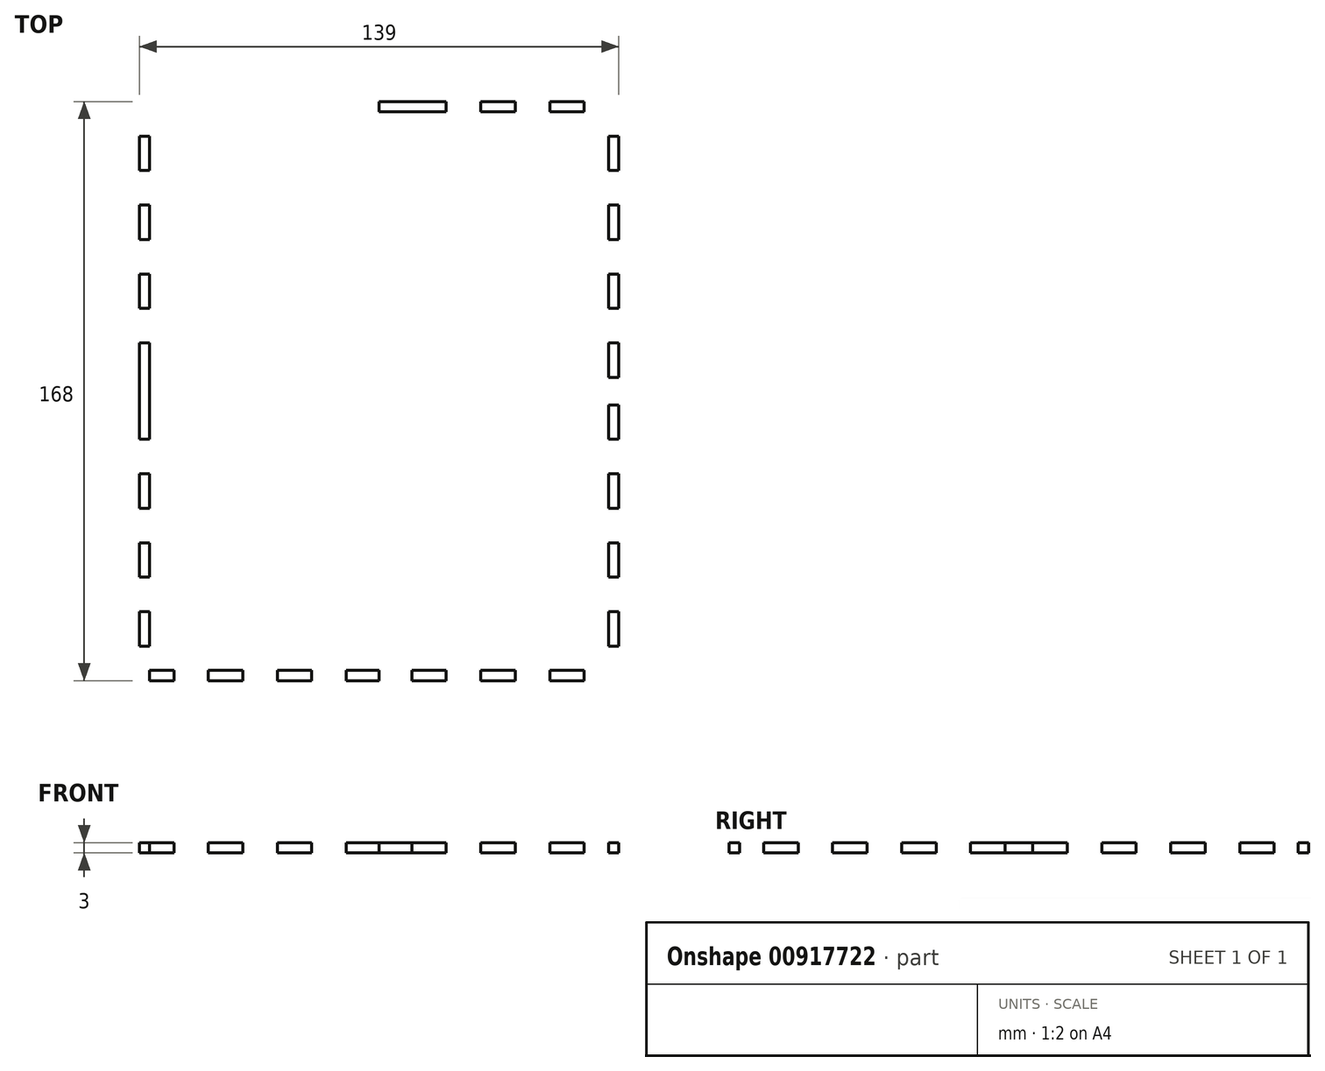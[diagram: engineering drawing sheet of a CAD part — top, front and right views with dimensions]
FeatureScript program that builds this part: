
annotation { "Feature Type Name" : "Feature", "Feature Type Description" : "" }
export const myFeature = defineFeature(function(context is Context, id is Id, definition is map)
    precondition{}
    {
        {
            var Q0;
            Q0=qCreatedBy(makeId("Top.planeOp"),FACE);
            var sketch = newSketch(context, id + "F0", { "sketchPlane" : qUnion([Q0])});
            skLineSegment(sketch, "E0.bottom", {"start": v(-69.5, 84) * mm, "end": v(0, 84) * mm});
            skLineSegment(sketch, "E0.top", {"start": v(-69.5, 0) * mm, "end": v(0, 0) * mm});
            skLineSegment(sketch, "E0.left", {"start": v(-69.5, 84) * mm, "end": v(-69.5, 0) * mm});
            skLineSegment(sketch, "E0.right", {"start": v(0, 84) * mm, "end": v(0, 0) * mm});
            skLineSegment(sketch, "E1", {"start": v(-69.5, 81) * mm, "end": v(0, 81) * mm});
            skLineSegment(sketch, "E2", {"start": v(-66.5, 84) * mm, "end": v(-66.5, 0) * mm});
            skLineSegment(sketch, "E3.bottom", {"start": v(-69.5, 84) * mm, "end": v(-59.5, 84) * mm});
            skLineSegment(sketch, "E3.top", {"start": v(-69.5, 81) * mm, "end": v(-59.5, 81) * mm});
            skLineSegment(sketch, "E3.left", {"start": v(-69.5, 84) * mm, "end": v(-69.5, 81) * mm});
            skLineSegment(sketch, "E3.right", {"start": v(-59.5, 84) * mm, "end": v(-59.5, 81) * mm});
            skLineSegment(sketch, "E4.bottom", {"start": v(-49.5, 84) * mm, "end": v(-39.5, 84) * mm});
            skLineSegment(sketch, "E4.top", {"start": v(-49.5, 81) * mm, "end": v(-39.5, 81) * mm});
            skLineSegment(sketch, "E4.left", {"start": v(-49.5, 84) * mm, "end": v(-49.5, 81) * mm});
            skLineSegment(sketch, "E4.right", {"start": v(-39.5, 84) * mm, "end": v(-39.5, 81) * mm});
            skLineSegment(sketch, "E5.bottom", {"start": v(-29.5, 84) * mm, "end": v(-19.5, 84) * mm});
            skLineSegment(sketch, "E5.top", {"start": v(-29.5, 81) * mm, "end": v(-19.5, 81) * mm});
            skLineSegment(sketch, "E5.left", {"start": v(-29.5, 84) * mm, "end": v(-29.5, 81) * mm});
            skLineSegment(sketch, "E5.right", {"start": v(-19.5, 84) * mm, "end": v(-19.5, 81) * mm});
            skLineSegment(sketch, "E6.bottom", {"start": v(-69.5, 84) * mm, "end": v(-66.5, 84) * mm});
            skLineSegment(sketch, "E6.top", {"start": v(-69.5, 74) * mm, "end": v(-66.5, 74) * mm});
            skLineSegment(sketch, "E6.left", {"start": v(-69.5, 84) * mm, "end": v(-69.5, 74) * mm});
            skLineSegment(sketch, "E6.right", {"start": v(-66.5, 84) * mm, "end": v(-66.5, 74) * mm});
            skLineSegment(sketch, "E7.bottom", {"start": v(-69.5, 64) * mm, "end": v(-66.5, 64) * mm});
            skLineSegment(sketch, "E7.top", {"start": v(-69.5, 54) * mm, "end": v(-66.5, 54) * mm});
            skLineSegment(sketch, "E7.left", {"start": v(-69.5, 64) * mm, "end": v(-69.5, 54) * mm});
            skLineSegment(sketch, "E7.right", {"start": v(-66.5, 64) * mm, "end": v(-66.5, 54) * mm});
            skLineSegment(sketch, "E8.bottom", {"start": v(-69.5, 44) * mm, "end": v(-66.5, 44) * mm});
            skLineSegment(sketch, "E8.top", {"start": v(-69.5, 34) * mm, "end": v(-66.5, 34) * mm});
            skLineSegment(sketch, "E8.left", {"start": v(-69.5, 44) * mm, "end": v(-69.5, 34) * mm});
            skLineSegment(sketch, "E8.right", {"start": v(-66.5, 44) * mm, "end": v(-66.5, 34) * mm});
            skLineSegment(sketch, "E9.bottom", {"start": v(-69.5, 24) * mm, "end": v(-66.5, 24) * mm});
            skLineSegment(sketch, "E9.top", {"start": v(-69.5, 14) * mm, "end": v(-66.5, 14) * mm});
            skLineSegment(sketch, "E9.left", {"start": v(-69.5, 24) * mm, "end": v(-69.5, 14) * mm});
            skLineSegment(sketch, "E9.right", {"start": v(-66.5, 24) * mm, "end": v(-66.5, 14) * mm});
            skLineSegment(sketch, "E10.bottom", {"start": v(-9.5, 84) * mm, "end": v(0, 84) * mm});
            skLineSegment(sketch, "E10.top", {"start": v(-9.5, 81) * mm, "end": v(0, 81) * mm});
            skLineSegment(sketch, "E10.left", {"start": v(-9.5, 84) * mm, "end": v(-9.5, 81) * mm});
            skLineSegment(sketch, "E10.right", {"start": v(0, 84) * mm, "end": v(0, 81) * mm});
            skLineSegment(sketch, "E11.MirrorCS", {"start": v(69.5, 84) * mm, "end": v(66.5, 84) * mm});
            skLineSegment(sketch, "E12.MirrorCS", {"start": v(69.5, 84) * mm, "end": v(69.5, 81) * mm});
            skLineSegment(sketch, "E13.MirrorCS", {"start": v(19.5, 84) * mm, "end": v(19.5, 81) * mm});
            skLineSegment(sketch, "E14.MirrorCS", {"start": v(69.5, 74) * mm, "end": v(66.5, 74) * mm});
            skLineSegment(sketch, "E15.MirrorCS", {"start": v(49.5, 84) * mm, "end": v(49.5, 81) * mm});
            skLineSegment(sketch, "E16.MirrorCS", {"start": v(69.5, 34) * mm, "end": v(66.5, 34) * mm});
            skLineSegment(sketch, "E17.MirrorCS", {"start": v(29.5, 84) * mm, "end": v(29.5, 81) * mm});
            skLineSegment(sketch, "E18.MirrorCS", {"start": v(69.5, 24) * mm, "end": v(66.5, 24) * mm});
            skLineSegment(sketch, "E19.MirrorCS", {"start": v(59.5, 84) * mm, "end": v(59.5, 81) * mm});
            skLineSegment(sketch, "E20.MirrorCS", {"start": v(39.5, 84) * mm, "end": v(39.5, 81) * mm});
            skLineSegment(sketch, "E21.MirrorCS", {"start": v(69.5, 54) * mm, "end": v(66.5, 54) * mm});
            skLineSegment(sketch, "E22.MirrorCS", {"start": v(69.5, 64) * mm, "end": v(66.5, 64) * mm});
            skLineSegment(sketch, "E23.MirrorCS", {"start": v(69.5, 14) * mm, "end": v(66.5, 14) * mm});
            skLineSegment(sketch, "E24.MirrorCS", {"start": v(9.5, 84) * mm, "end": v(9.5, 81) * mm});
            skLineSegment(sketch, "E25.MirrorCS", {"start": v(69.5, 44) * mm, "end": v(66.5, 44) * mm});
            skLineSegment(sketch, "E26.MirrorCS", {"start": v(69.5, 64) * mm, "end": v(69.5, 54) * mm});
            skLineSegment(sketch, "E27.MirrorCS", {"start": v(66.5, 64) * mm, "end": v(66.5, 54) * mm});
            skLineSegment(sketch, "E28.MirrorCS", {"start": v(69.5, 44) * mm, "end": v(69.5, 34) * mm});
            skLineSegment(sketch, "E29.MirrorCS", {"start": v(69.5, 84) * mm, "end": v(59.5, 84) * mm});
            skLineSegment(sketch, "E30.MirrorCS", {"start": v(29.5, 84) * mm, "end": v(19.5, 84) * mm});
            skLineSegment(sketch, "E31.MirrorCS", {"start": v(69.5, 0) * mm, "end": v(0, 0) * mm});
            skLineSegment(sketch, "E32.MirrorCS", {"start": v(69.5, 81) * mm, "end": v(0, 81) * mm});
            skLineSegment(sketch, "E33.MirrorCS", {"start": v(66.5, 84) * mm, "end": v(66.5, 0) * mm});
            skLineSegment(sketch, "E34.MirrorCS", {"start": v(9.5, 84) * mm, "end": v(0, 84) * mm});
            skLineSegment(sketch, "E35.MirrorCS", {"start": v(66.5, 24) * mm, "end": v(66.5, 14) * mm});
            skLineSegment(sketch, "E36.MirrorCS", {"start": v(49.5, 81) * mm, "end": v(39.5, 81) * mm});
            skLineSegment(sketch, "E37.MirrorCS", {"start": v(69.5, 84) * mm, "end": v(0, 84) * mm});
            skLineSegment(sketch, "E38.MirrorCS", {"start": v(29.5, 81) * mm, "end": v(19.5, 81) * mm});
            skLineSegment(sketch, "E39.MirrorCS", {"start": v(9.5, 81) * mm, "end": v(0, 81) * mm});
            skLineSegment(sketch, "E40.MirrorCS", {"start": v(49.5, 84) * mm, "end": v(39.5, 84) * mm});
            skLineSegment(sketch, "E41.MirrorCS", {"start": v(69.5, 84) * mm, "end": v(69.5, 0) * mm});
            skLineSegment(sketch, "E42.MirrorCS", {"start": v(69.5, 24) * mm, "end": v(69.5, 14) * mm});
            skLineSegment(sketch, "E43.MirrorCS", {"start": v(66.5, 84) * mm, "end": v(66.5, 74) * mm});
            skLineSegment(sketch, "E44.MirrorCS", {"start": v(69.5, 84) * mm, "end": v(69.5, 74) * mm});
            skLineSegment(sketch, "E45.MirrorCS", {"start": v(66.5, 44) * mm, "end": v(66.5, 34) * mm});
            skLineSegment(sketch, "E46.MirrorCS", {"start": v(69.5, 81) * mm, "end": v(59.5, 81) * mm});
            skLineSegment(sketch, "E47.bottom", {"start": v(-69.5, 4) * mm, "end": v(-66.5, 4) * mm});
            skLineSegment(sketch, "E47.top", {"start": v(-69.5, 0) * mm, "end": v(-66.5, 0) * mm});
            skLineSegment(sketch, "E47.left", {"start": v(-69.5, 4) * mm, "end": v(-69.5, 0) * mm});
            skLineSegment(sketch, "E47.right", {"start": v(-66.5, 4) * mm, "end": v(-66.5, 0) * mm});
            skLineSegment(sketch, "E48.MirrorCS", {"start": v(69.5, 4) * mm, "end": v(69.5, 0) * mm});
            skLineSegment(sketch, "E49.MirrorCS", {"start": v(69.5, 0) * mm, "end": v(66.5, 0) * mm});
            skLineSegment(sketch, "E50.MirrorCS", {"start": v(66.5, 4) * mm, "end": v(66.5, 0) * mm});
            skLineSegment(sketch, "E51.MirrorCS", {"start": v(69.5, 4) * mm, "end": v(66.5, 4) * mm});
            skLineSegment(sketch, "E52.MirrorCS", {"start": v(0, -84) * mm, "end": v(0, -81) * mm});
            skLineSegment(sketch, "E53.MirrorCS", {"start": v(-69.5, -84) * mm, "end": v(-69.5, -81) * mm});
            skLineSegment(sketch, "E54.MirrorCS", {"start": v(-69.5, -84) * mm, "end": v(-66.5, -84) * mm});
            skLineSegment(sketch, "E55.MirrorCS", {"start": v(69.5, -84) * mm, "end": v(69.5, -81) * mm});
            skLineSegment(sketch, "E56.MirrorCS", {"start": v(69.5, -84) * mm, "end": v(66.5, -84) * mm});
            skLineSegment(sketch, "E57.MirrorCS", {"start": v(-39.5, -84) * mm, "end": v(-39.5, -81) * mm});
            skLineSegment(sketch, "E58.MirrorCS", {"start": v(69.5, -34) * mm, "end": v(66.5, -34) * mm});
            skLineSegment(sketch, "E59.MirrorCS", {"start": v(69.5, -54) * mm, "end": v(66.5, -54) * mm});
            skLineSegment(sketch, "E60.MirrorCS", {"start": v(66.5, -4) * mm, "end": v(66.5, 0) * mm});
            skLineSegment(sketch, "E61.MirrorCS", {"start": v(39.5, -84) * mm, "end": v(39.5, -81) * mm});
            skLineSegment(sketch, "E62.MirrorCS", {"start": v(69.5, -64) * mm, "end": v(66.5, -64) * mm});
            skLineSegment(sketch, "E63.MirrorCS", {"start": v(59.5, -84) * mm, "end": v(59.5, -81) * mm});
            skLineSegment(sketch, "E64.MirrorCS", {"start": v(19.5, -84) * mm, "end": v(19.5, -81) * mm});
            skLineSegment(sketch, "E65.MirrorCS", {"start": v(-66.5, -4) * mm, "end": v(-66.5, 0) * mm});
            skLineSegment(sketch, "E66.MirrorCS", {"start": v(-69.5, -44) * mm, "end": v(-66.5, -44) * mm});
            skLineSegment(sketch, "E67.MirrorCS", {"start": v(69.5, -4) * mm, "end": v(66.5, -4) * mm});
            skLineSegment(sketch, "E68.MirrorCS", {"start": v(-69.5, -74) * mm, "end": v(-66.5, -74) * mm});
            skLineSegment(sketch, "E69.MirrorCS", {"start": v(9.5, -84) * mm, "end": v(9.5, -81) * mm});
            skLineSegment(sketch, "E70.MirrorCS", {"start": v(29.5, -84) * mm, "end": v(29.5, -81) * mm});
            skLineSegment(sketch, "E71.MirrorCS", {"start": v(-29.5, -84) * mm, "end": v(-29.5, -81) * mm});
            skLineSegment(sketch, "E72.MirrorCS", {"start": v(-69.5, -64) * mm, "end": v(-66.5, -64) * mm});
            skLineSegment(sketch, "E73.MirrorCS", {"start": v(-59.5, -84) * mm, "end": v(-59.5, -81) * mm});
            skLineSegment(sketch, "E74.MirrorCS", {"start": v(69.5, -44) * mm, "end": v(66.5, -44) * mm});
            skLineSegment(sketch, "E75.MirrorCS", {"start": v(69.5, -4) * mm, "end": v(69.5, 0) * mm});
            skLineSegment(sketch, "E76.MirrorCS", {"start": v(-69.5, -4) * mm, "end": v(-69.5, 0) * mm});
            skLineSegment(sketch, "E77.MirrorCS", {"start": v(-69.5, -4) * mm, "end": v(-66.5, -4) * mm});
            skLineSegment(sketch, "E78.MirrorCS", {"start": v(-19.5, -84) * mm, "end": v(-19.5, -81) * mm});
            skLineSegment(sketch, "E79.MirrorCS", {"start": v(69.5, -14) * mm, "end": v(66.5, -14) * mm});
            skLineSegment(sketch, "E80.MirrorCS", {"start": v(-69.5, -54) * mm, "end": v(-66.5, -54) * mm});
            skLineSegment(sketch, "E81.MirrorCS", {"start": v(-9.5, -84) * mm, "end": v(-9.5, -81) * mm});
            skLineSegment(sketch, "E82.MirrorCS", {"start": v(69.5, -24) * mm, "end": v(66.5, -24) * mm});
            skLineSegment(sketch, "E83.MirrorCS", {"start": v(69.5, -74) * mm, "end": v(66.5, -74) * mm});
            skLineSegment(sketch, "E84.MirrorCS", {"start": v(-69.5, -24) * mm, "end": v(-66.5, -24) * mm});
            skLineSegment(sketch, "E85.MirrorCS", {"start": v(-49.5, -84) * mm, "end": v(-49.5, -81) * mm});
            skLineSegment(sketch, "E86.MirrorCS", {"start": v(-69.5, -14) * mm, "end": v(-66.5, -14) * mm});
            skLineSegment(sketch, "E87.MirrorCS", {"start": v(49.5, -84) * mm, "end": v(49.5, -81) * mm});
            skLineSegment(sketch, "E88.MirrorCS", {"start": v(-69.5, -34) * mm, "end": v(-66.5, -34) * mm});
            skLineSegment(sketch, "E89.MirrorCS", {"start": v(-69.5, -64) * mm, "end": v(-69.5, -54) * mm});
            skLineSegment(sketch, "E90.MirrorCS", {"start": v(69.5, -44) * mm, "end": v(69.5, -34) * mm});
            skLineSegment(sketch, "E91.MirrorCS", {"start": v(69.5, -24) * mm, "end": v(69.5, -14) * mm});
            skLineSegment(sketch, "E92.MirrorCS", {"start": v(69.5, -84) * mm, "end": v(59.5, -84) * mm});
            skLineSegment(sketch, "E93.MirrorCS", {"start": v(66.5, -64) * mm, "end": v(66.5, -54) * mm});
            skLineSegment(sketch, "E94.MirrorCS", {"start": v(66.5, -84) * mm, "end": v(66.5, -74) * mm});
            skLineSegment(sketch, "E95.MirrorCS", {"start": v(29.5, -84) * mm, "end": v(19.5, -84) * mm});
            skLineSegment(sketch, "E96.MirrorCS", {"start": v(66.5, -44) * mm, "end": v(66.5, -34) * mm});
            skLineSegment(sketch, "E97.MirrorCS", {"start": v(49.5, -84) * mm, "end": v(39.5, -84) * mm});
            skLineSegment(sketch, "E98.MirrorCS", {"start": v(69.5, -84) * mm, "end": v(69.5, -74) * mm});
            skLineSegment(sketch, "E99.MirrorCS", {"start": v(-66.5, -64) * mm, "end": v(-66.5, -54) * mm});
            skLineSegment(sketch, "E100.MirrorCS", {"start": v(69.5, -64) * mm, "end": v(69.5, -54) * mm});
            skLineSegment(sketch, "E101.MirrorCS", {"start": v(9.5, -84) * mm, "end": v(0, -84) * mm});
            skLineSegment(sketch, "E102.MirrorCS", {"start": v(-69.5, -44) * mm, "end": v(-69.5, -34) * mm});
            skLineSegment(sketch, "E103.MirrorCS", {"start": v(-29.5, -84) * mm, "end": v(-19.5, -84) * mm});
            skLineSegment(sketch, "E104.MirrorCS", {"start": v(-29.5, -81) * mm, "end": v(-19.5, -81) * mm});
            skLineSegment(sketch, "E105.MirrorCS", {"start": v(49.5, -81) * mm, "end": v(39.5, -81) * mm});
            skLineSegment(sketch, "E106.MirrorCS", {"start": v(-69.5, -84) * mm, "end": v(0, -84) * mm});
            skLineSegment(sketch, "E107.MirrorCS", {"start": v(-66.5, -44) * mm, "end": v(-66.5, -34) * mm});
            skLineSegment(sketch, "E108.MirrorCS", {"start": v(29.5, -81) * mm, "end": v(19.5, -81) * mm});
            skLineSegment(sketch, "E109.MirrorCS", {"start": v(-66.5, -84) * mm, "end": v(-66.5, -74) * mm});
            skLineSegment(sketch, "E110.MirrorCS", {"start": v(-9.5, -81) * mm, "end": v(0, -81) * mm});
            skLineSegment(sketch, "E111.MirrorCS", {"start": v(69.5, -81) * mm, "end": v(0, -81) * mm});
            skLineSegment(sketch, "E112.MirrorCS", {"start": v(-69.5, -84) * mm, "end": v(-69.5, 0) * mm});
            skLineSegment(sketch, "E113.MirrorCS", {"start": v(-49.5, -84) * mm, "end": v(-39.5, -84) * mm});
            skLineSegment(sketch, "E114.MirrorCS", {"start": v(9.5, -81) * mm, "end": v(0, -81) * mm});
            skLineSegment(sketch, "E115.MirrorCS", {"start": v(66.5, -84) * mm, "end": v(66.5, 0) * mm});
            skLineSegment(sketch, "E116.MirrorCS", {"start": v(69.5, -84) * mm, "end": v(0, -84) * mm});
            skLineSegment(sketch, "E117.MirrorCS", {"start": v(-9.5, -84) * mm, "end": v(0, -84) * mm});
            skLineSegment(sketch, "E118.MirrorCS", {"start": v(0, -84) * mm, "end": v(0, 0) * mm});
            skLineSegment(sketch, "E119.MirrorCS", {"start": v(-69.5, -81) * mm, "end": v(0, -81) * mm});
            skLineSegment(sketch, "E120.MirrorCS", {"start": v(-49.5, -81) * mm, "end": v(-39.5, -81) * mm});
            skLineSegment(sketch, "E121.MirrorCS", {"start": v(66.5, -24) * mm, "end": v(66.5, -14) * mm});
            skLineSegment(sketch, "E122.MirrorCS", {"start": v(-66.5, -24) * mm, "end": v(-66.5, -14) * mm});
            skLineSegment(sketch, "E123.MirrorCS", {"start": v(-69.5, -24) * mm, "end": v(-69.5, -14) * mm});
            skLineSegment(sketch, "E124.MirrorCS", {"start": v(-69.5, -84) * mm, "end": v(-59.5, -84) * mm});
            skLineSegment(sketch, "E125.MirrorCS", {"start": v(69.5, -81) * mm, "end": v(59.5, -81) * mm});
            skLineSegment(sketch, "E126.MirrorCS", {"start": v(-66.5, -84) * mm, "end": v(-66.5, 0) * mm});
            skLineSegment(sketch, "E127.MirrorCS", {"start": v(69.5, -84) * mm, "end": v(69.5, 0) * mm});
            skLineSegment(sketch, "E128.MirrorCS", {"start": v(-69.5, -84) * mm, "end": v(-69.5, -74) * mm});
            skLineSegment(sketch, "E129.MirrorCS", {"start": v(-69.5, -81) * mm, "end": v(-59.5, -81) * mm});
            skSolve(sketch);
        }
        {
            var Q0;
            Q0=makeQuery(id+"F0.imprint","IMPRINT",FACE,{"disambiguationData":[TD([[makeQuery(id+"F0.imprint","IMPRINT",EDGE,{"derivedFrom":sQuery(id+"F0.wireOp",EDGE,"E0.top")}),1.0]])]});
            var Q1;
            {var subQ10=sQuery(id+"F0.wireOp",EDGE,"E0.right");Q1=makeQuery(id+"F0.imprint","IMPRINT",FACE,{"disambiguationData":[TD([[makeQuery(id+"F0.imprint","IMPRINT",EDGE,{"derivedFrom":subQ10}),1.0]])]});}
            var Q2;
            {var subQ7=sQuery(id+"F0.wireOp",EDGE,"E114.MirrorCS");Q2=makeQuery(id+"F0.imprint","IMPRINT",FACE,{"disambiguationData":[TD([[makeQuery(id+"F0.imprint","IMPRINT",EDGE,{"derivedFrom":subQ7}),-1.0]])]});}
            var Q3;
            {var subQ12=sQuery(id+"F0.wireOp",EDGE,"E0.top");Q3=makeQuery(id+"F0.imprint","IMPRINT",FACE,{"disambiguationData":[TD([[makeQuery(id+"F0.imprint","IMPRINT",EDGE,{"derivedFrom":subQ12}),-1.0]])]});}
            var Q4;
            {var subQ0=sQuery(id+"F0.wireOp",EDGE,"E3.bottom");Q4=makeQuery(id+"F0.imprint","IMPRINT",FACE,{"disambiguationData":[TD([[makeQuery(id+"F0.imprint","IMPRINT",EDGE,{"derivedFrom":subQ0}),-1.0]])]});}
            var Q5;
            Q5=makeQuery(id+"F0.imprint","IMPRINT",FACE,{"disambiguationData":[TD([[makeQuery(id+"F0.imprint","IMPRINT",EDGE,{"derivedFrom":sQuery(id+"F0.wireOp",EDGE,"E4.bottom")}),-1.0]])]});
            var Q6;
            Q6=makeQuery(id+"F0.imprint","IMPRINT",FACE,{"disambiguationData":[TD([[makeQuery(id+"F0.imprint","IMPRINT",EDGE,{"derivedFrom":sQuery(id+"F0.wireOp",EDGE,"E5.bottom")}),-1.0]])]});
            var Q7;
            Q7=makeQuery(id+"F0.imprint","IMPRINT",FACE,{"disambiguationData":[TD([[makeQuery(id+"F0.imprint","IMPRINT",EDGE,{"derivedFrom":sQuery(id+"F0.wireOp",EDGE,"E10.bottom")}),-1.0]])]});
            var Q8;
            {var subQ0=sQuery(id+"F0.wireOp",EDGE,"E13.MirrorCS");Q8=makeQuery(id+"F0.imprint","IMPRINT",FACE,{"disambiguationData":[TD([[makeQuery(id+"F0.imprint","IMPRINT",EDGE,{"derivedFrom":subQ0}),-1.0]])]});}
            var Q9;
            {var subQ0=sQuery(id+"F0.wireOp",EDGE,"E17.MirrorCS");Q9=makeQuery(id+"F0.imprint","IMPRINT",FACE,{"disambiguationData":[TD([[makeQuery(id+"F0.imprint","IMPRINT",EDGE,{"derivedFrom":subQ0}),1.0]])]});}
            var Q10;
            {var subQ0=sQuery(id+"F0.wireOp",EDGE,"E15.MirrorCS");Q10=makeQuery(id+"F0.imprint","IMPRINT",FACE,{"disambiguationData":[TD([[makeQuery(id+"F0.imprint","IMPRINT",EDGE,{"derivedFrom":subQ0}),1.0]])]});}
            var Q11;
            {var subQ0=sQuery(id+"F0.wireOp",EDGE,"E14.MirrorCS");Q11=makeQuery(id+"F0.imprint","IMPRINT",FACE,{"disambiguationData":[TD([[makeQuery(id+"F0.imprint","IMPRINT",EDGE,{"derivedFrom":subQ0}),1.0]])]});}
            var Q12;
            {var subQ0=sQuery(id+"F0.wireOp",EDGE,"E6.top");Q12=makeQuery(id+"F0.imprint","IMPRINT",FACE,{"disambiguationData":[TD([[makeQuery(id+"F0.imprint","IMPRINT",EDGE,{"derivedFrom":subQ0}),-1.0]])]});}
            var Q13;
            {var subQ0=sQuery(id+"F0.wireOp",EDGE,"E7.top");Q13=makeQuery(id+"F0.imprint","IMPRINT",FACE,{"disambiguationData":[TD([[makeQuery(id+"F0.imprint","IMPRINT",EDGE,{"derivedFrom":subQ0}),-1.0]])]});}
            var Q14;
            {var subQ0=sQuery(id+"F0.wireOp",EDGE,"E8.top");Q14=makeQuery(id+"F0.imprint","IMPRINT",FACE,{"disambiguationData":[TD([[makeQuery(id+"F0.imprint","IMPRINT",EDGE,{"derivedFrom":subQ0}),-1.0]])]});}
            var Q15;
            {var subQ2=sQuery(id+"F0.wireOp",EDGE,"E9.top");Q15=makeQuery(id+"F0.imprint","IMPRINT",FACE,{"disambiguationData":[TD([[makeQuery(id+"F0.imprint","IMPRINT",EDGE,{"derivedFrom":subQ2}),-1.0]])]});}
            var Q16;
            {var subQ0=sQuery(id+"F0.wireOp",EDGE,"E77.MirrorCS");Q16=makeQuery(id+"F0.imprint","IMPRINT",FACE,{"disambiguationData":[TD([[makeQuery(id+"F0.imprint","IMPRINT",EDGE,{"derivedFrom":subQ0}),-1.0]])]});}
            var Q17;
            {var subQ0=sQuery(id+"F0.wireOp",EDGE,"E84.MirrorCS");Q17=makeQuery(id+"F0.imprint","IMPRINT",FACE,{"disambiguationData":[TD([[makeQuery(id+"F0.imprint","IMPRINT",EDGE,{"derivedFrom":subQ0}),-1.0]])]});}
            var Q18;
            {var subQ0=sQuery(id+"F0.wireOp",EDGE,"E66.MirrorCS");Q18=makeQuery(id+"F0.imprint","IMPRINT",FACE,{"disambiguationData":[TD([[makeQuery(id+"F0.imprint","IMPRINT",EDGE,{"derivedFrom":subQ0}),-1.0]])]});}
            var Q19;
            {var subQ0=sQuery(id+"F0.wireOp",EDGE,"E68.MirrorCS");Q19=makeQuery(id+"F0.imprint","IMPRINT",FACE,{"disambiguationData":[TD([[makeQuery(id+"F0.imprint","IMPRINT",EDGE,{"derivedFrom":subQ0}),1.0]])]});}
            var Q20;
            {var subQ0=sQuery(id+"F0.wireOp",EDGE,"E62.MirrorCS");Q20=makeQuery(id+"F0.imprint","IMPRINT",FACE,{"disambiguationData":[TD([[makeQuery(id+"F0.imprint","IMPRINT",EDGE,{"derivedFrom":subQ0}),1.0]])]});}
            var Q21;
            {var subQ0=sQuery(id+"F0.wireOp",EDGE,"E59.MirrorCS");Q21=makeQuery(id+"F0.imprint","IMPRINT",FACE,{"disambiguationData":[TD([[makeQuery(id+"F0.imprint","IMPRINT",EDGE,{"derivedFrom":subQ0}),-1.0]])]});}
            var Q22;
            {var subQ0=sQuery(id+"F0.wireOp",EDGE,"E58.MirrorCS");Q22=makeQuery(id+"F0.imprint","IMPRINT",FACE,{"disambiguationData":[TD([[makeQuery(id+"F0.imprint","IMPRINT",EDGE,{"derivedFrom":subQ0}),-1.0]])]});}
            var Q23;
            {var subQ0=sQuery(id+"F0.wireOp",EDGE,"E67.MirrorCS");Q23=makeQuery(id+"F0.imprint","IMPRINT",FACE,{"disambiguationData":[TD([[makeQuery(id+"F0.imprint","IMPRINT",EDGE,{"derivedFrom":subQ0}),1.0]])]});}
            var Q24;
            {var subQ0=sQuery(id+"F0.wireOp",EDGE,"E23.MirrorCS");Q24=makeQuery(id+"F0.imprint","IMPRINT",FACE,{"disambiguationData":[TD([[makeQuery(id+"F0.imprint","IMPRINT",EDGE,{"derivedFrom":subQ0}),1.0]])]});}
            var Q25;
            {var subQ0=sQuery(id+"F0.wireOp",EDGE,"E21.MirrorCS");Q25=makeQuery(id+"F0.imprint","IMPRINT",FACE,{"disambiguationData":[TD([[makeQuery(id+"F0.imprint","IMPRINT",EDGE,{"derivedFrom":subQ0}),1.0]])]});}
            var Q26;
            {var subQ0=sQuery(id+"F0.wireOp",EDGE,"E16.MirrorCS");Q26=makeQuery(id+"F0.imprint","IMPRINT",FACE,{"disambiguationData":[TD([[makeQuery(id+"F0.imprint","IMPRINT",EDGE,{"derivedFrom":subQ0}),1.0]])]});}
            var Q27;
            {var subQ0=sQuery(id+"F0.wireOp",EDGE,"E73.MirrorCS");Q27=makeQuery(id+"F0.imprint","IMPRINT",FACE,{"disambiguationData":[TD([[makeQuery(id+"F0.imprint","IMPRINT",EDGE,{"derivedFrom":subQ0}),1.0]])]});}
            var Q28;
            Q28=makeQuery(id+"F0.imprint","IMPRINT",FACE,{"disambiguationData":[TD([[makeQuery(id+"F0.imprint","IMPRINT",EDGE,{"derivedFrom":sQuery(id+"F0.wireOp",EDGE,"E57.MirrorCS")}),1.0]])]});
            var Q29;
            {var subQ0=sQuery(id+"F0.wireOp",EDGE,"E71.MirrorCS");Q29=makeQuery(id+"F0.imprint","IMPRINT",FACE,{"disambiguationData":[TD([[makeQuery(id+"F0.imprint","IMPRINT",EDGE,{"derivedFrom":subQ0}),-1.0]])]});}
            var Q30;
            {var subQ0=sQuery(id+"F0.wireOp",EDGE,"E81.MirrorCS");Q30=makeQuery(id+"F0.imprint","IMPRINT",FACE,{"disambiguationData":[TD([[makeQuery(id+"F0.imprint","IMPRINT",EDGE,{"derivedFrom":subQ0}),-1.0]])]});}
            var Q31;
            {var subQ0=sQuery(id+"F0.wireOp",EDGE,"E64.MirrorCS");Q31=makeQuery(id+"F0.imprint","IMPRINT",FACE,{"disambiguationData":[TD([[makeQuery(id+"F0.imprint","IMPRINT",EDGE,{"derivedFrom":subQ0}),1.0]])]});}
            var Q32;
            {var subQ0=sQuery(id+"F0.wireOp",EDGE,"E61.MirrorCS");Q32=makeQuery(id+"F0.imprint","IMPRINT",FACE,{"disambiguationData":[TD([[makeQuery(id+"F0.imprint","IMPRINT",EDGE,{"derivedFrom":subQ0}),1.0]])]});}
            var Q33;
            {var subQ0=sQuery(id+"F0.wireOp",EDGE,"E63.MirrorCS");Q33=makeQuery(id+"F0.imprint","IMPRINT",FACE,{"disambiguationData":[TD([[makeQuery(id+"F0.imprint","IMPRINT",EDGE,{"derivedFrom":subQ0}),1.0]])]});}
            extrude(context, id + "F1", {"entities" : qUnion([Q0, Q1, Q2, Q3, Q4, Q5, Q6, Q7, Q8, Q9, Q10, Q11, Q12, Q13, Q14, Q15, Q16, Q17, Q18, Q19, Q20, Q21, Q22, Q23, Q24, Q25, Q26, Q27, Q28, Q29, Q30, Q31, Q32, Q33]), "depth" : 3 * mm, "offsetDistance" : 25 * mm, "symmetric" : true});
        }
    });
